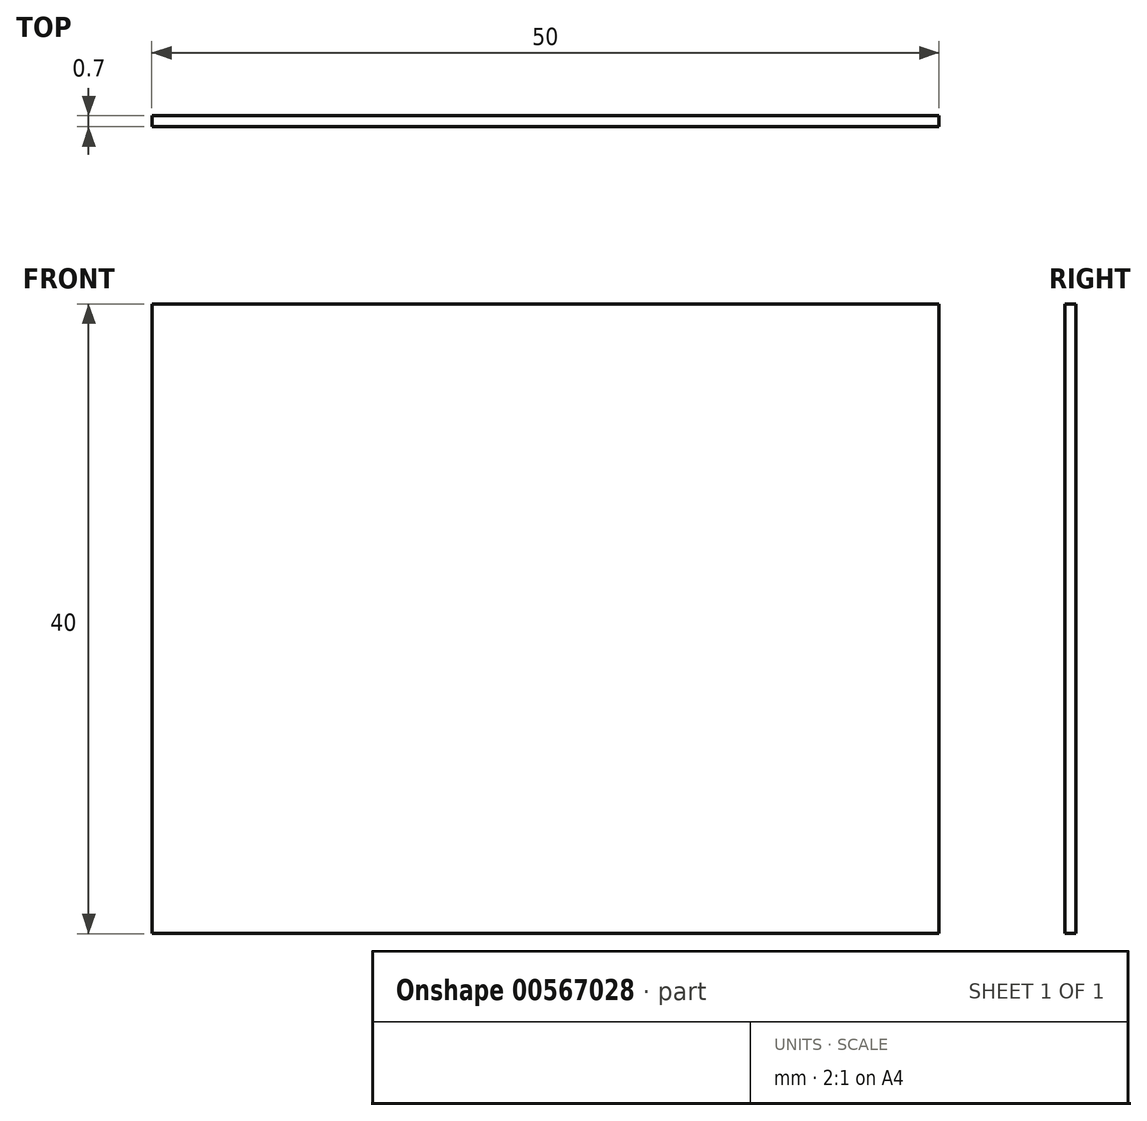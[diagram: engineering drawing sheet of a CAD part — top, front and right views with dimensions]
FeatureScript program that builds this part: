
annotation { "Feature Type Name" : "Feature", "Feature Type Description" : "" }
export const myFeature = defineFeature(function(context is Context, id is Id, definition is map)
    precondition{}
    {
        {
            var Q0;
            Q0=qCreatedBy(makeId("Front.planeOp"),FACE);
            var sketch = newSketch(context, id + "F0", { "sketchPlane" : qUnion([Q0])});
            skLineSegment(sketch, "E0.bottom", {"start": v(-74.65, 74.43) * mm, "end": v(-24.65, 74.43) * mm});
            skLineSegment(sketch, "E0.top", {"start": v(-74.65, 34.43) * mm, "end": v(-24.65, 34.43) * mm});
            skLineSegment(sketch, "E0.left", {"start": v(-74.65, 74.43) * mm, "end": v(-74.65, 34.43) * mm});
            skLineSegment(sketch, "E0.right", {"start": v(-24.65, 74.43) * mm, "end": v(-24.65, 34.43) * mm});
            skSolve(sketch);
        }
        {
            var Q0;
            Q0 = qSketchRegion(id + "F0", true);
            extrude(context, id + "F1", {"entities" : qUnion([Q0]), "depth" : 0.7 * mm, "offsetDistance" : 25 * mm});
        }
    });
